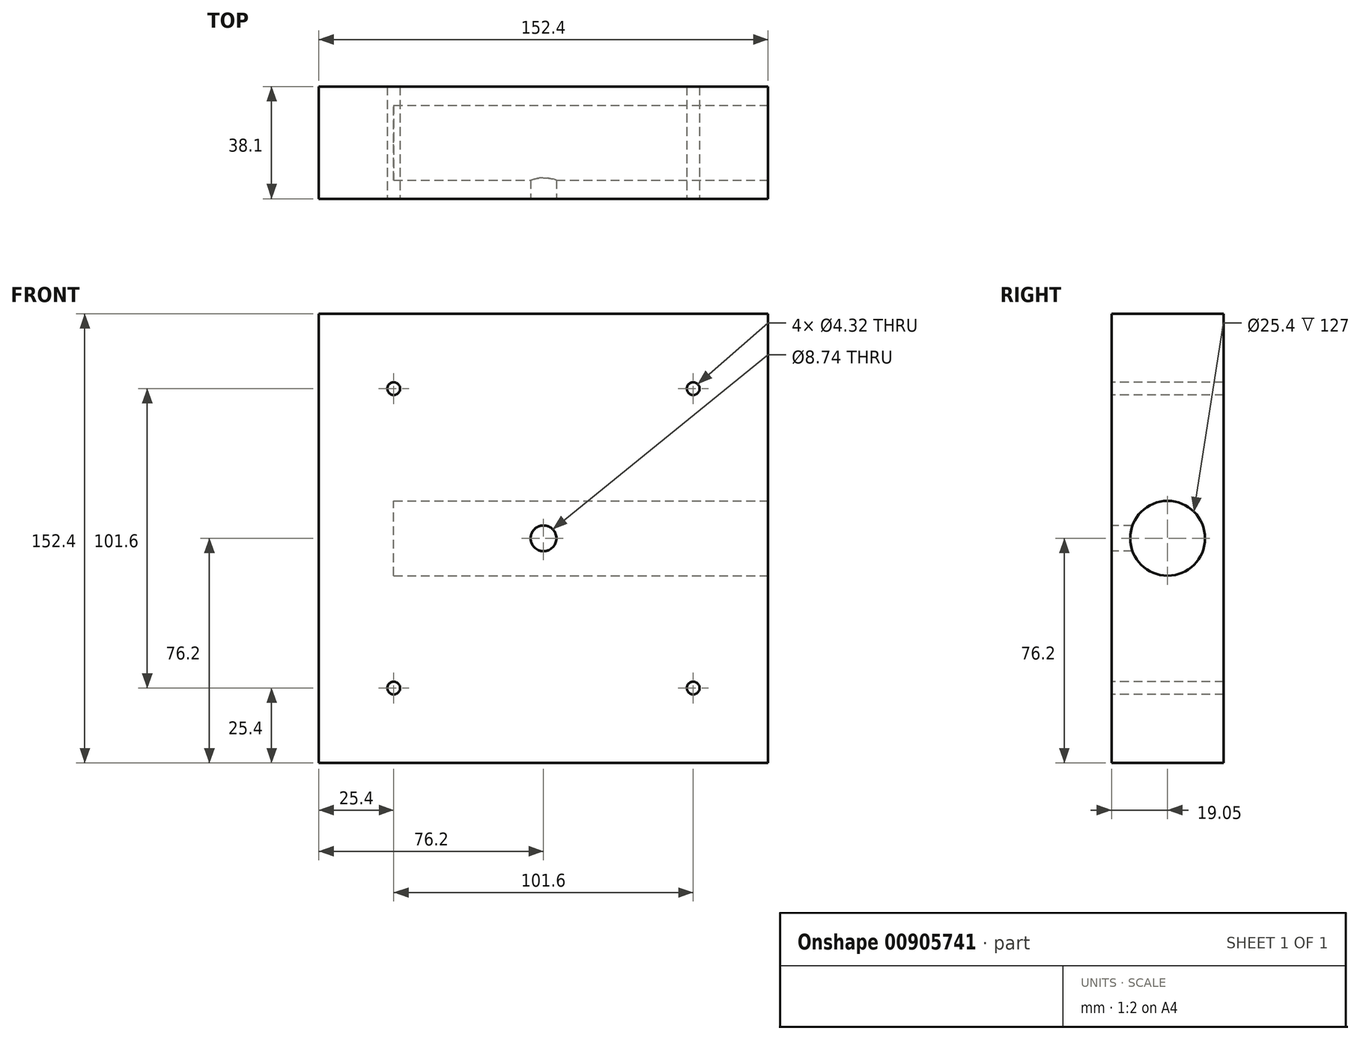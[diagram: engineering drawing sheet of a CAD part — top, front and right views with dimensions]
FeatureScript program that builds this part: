
annotation { "Feature Type Name" : "Feature", "Feature Type Description" : "" }
export const myFeature = defineFeature(function(context is Context, id is Id, definition is map)
    precondition{}
    {
        {
            var Q0;
            Q0=qCreatedBy(makeId("Front.planeOp"),FACE);
            var sketch = newSketch(context, id + "F0", { "sketchPlane" : qUnion([Q0])});
            skLineSegment(sketch, "E0.bottom", {"start": v(76.2, -76.2) * mm, "end": v(-76.2, -76.2) * mm});
            skLineSegment(sketch, "E0.top", {"start": v(76.2, 76.2) * mm, "end": v(-76.2, 76.2) * mm});
            skLineSegment(sketch, "E0.left", {"start": v(76.2, -76.2) * mm, "end": v(76.2, 76.2) * mm});
            skLineSegment(sketch, "E0.right", {"start": v(-76.2, -76.2) * mm, "end": v(-76.2, 76.2) * mm});
            skPoint(sketch, "E0.middle", {"position": v(0, 0) * mm});
            skSolve(sketch);
        }
        {
            var Q0;
            Q0=makeQuery(id+"F0.imprint","IMPRINT",FACE,{"disambiguationData":[TD([[makeQuery(id+"F0.imprint","IMPRINT",EDGE,{"derivedFrom":sQuery(id+"F0.wireOp",EDGE,"E0.bottom")}),-1.0]])]});
            extrude(context, id + "F1", {"entities" : qUnion([Q0]), "depth" : 38.1 * mm, "offsetDistance" : 25.4 * mm});
        }
        {
            var Q0;
            Q0=makeQuery(id+"F1.opExtrude","SWEPT_FACE",FACE,{"disambiguationData":[OSD([sQuery(id+"F0.wireOp",EDGE,"E0.left")])]});
            var sketch = newSketch(context, id + "F2", { "sketchPlane" : qUnion([Q0])});
            skCircle(sketch, "E1", {"center": v(-19.05, 0) * mm, "radius": 12.7 * mm});
            skPoint(sketch, "E1.centerSnap0", {"position": v(-19.05, 76.2) * mm});
            skSolve(sketch);
        }
        {
            var Q0;
            Q0=makeQuery(id+"F1.opExtrude","CAP_FACE",FACE,{"disambiguationData":[OSD([sQuery(id+"F0.wireOp",EDGE,"E0.bottom"),sQuery(id+"F0.wireOp",EDGE,"E0.top"),sQuery(id+"F0.wireOp",EDGE,"E0.left"),sQuery(id+"F0.wireOp",EDGE,"E0.right")])],"isStart":false});
            var sketch = newSketch(context, id + "F3", { "sketchPlane" : qUnion([Q0])});
            skCircle(sketch, "E2", {"center": v(0, 0) * mm, "radius": 1.27 * mm});
            skSolve(sketch);
        }
        {
            var Q0;
            Q0=sQuery(id+"F3.wireOp",VERTEX,"E2.center");
            var Q1;
            Q1=makeQuery(id+"F1.opExtrude","SWEPT_BODY",BODY,{"disambiguationData":[OSD([sQuery(id+"F0.wireOp",EDGE,"E0.bottom"),sQuery(id+"F0.wireOp",EDGE,"E0.top"),sQuery(id+"F0.wireOp",EDGE,"E0.left"),sQuery(id+"F0.wireOp",EDGE,"E0.right")])]});
            hole(context, id + "F4", {"style" : HoleStyle.SIMPLE, "endStyle" : HoleEndStyle.BLIND, "standardTappedOrClearance" : lookupTablePath({ "fit" : "Normal (ASME)", "standard" : "ANSI", "size" : "5/16", "type" : "Clearance" }), "standardBlindInLast" : lookupTablePath({ "fit" : "Normal", "standard" : "ANSI", "size" : "5/16", "type" : "Clearance" }), "holeDiameter" : 8.74 * mm, "majorDiameter" : 6.35 * mm, "holeDepth" : 12.7 * mm, "isTappedThrough" : true, "tappedDepth" : 12.7 * mm, "tapClearance" : 3, "locations" : qUnion([Q0]), "scope" : qUnion([Q1])});
        }
        {
            var Q0;
            Q0=makeQuery(id+"F2.imprint","IMPRINT",FACE,{"disambiguationData":[TD([[makeQuery(id+"F2.imprint","IMPRINT",EDGE,{"derivedFrom":sQuery(id+"F2.wireOp",EDGE,"E1")}),1.0]])]});
            extrude(context, id + "F5", {"entities" : qUnion([Q0]), "operationType" : NewBodyOperationType.REMOVE, "oppositeDirection" : true, "depth" : 127 * mm, "offsetDistance" : 25.4 * mm});
        }
        {
            var Q0;
            Q0=makeQuery(id+"F1.opExtrude","CAP_FACE",FACE,{"disambiguationData":[OSD([sQuery(id+"F0.wireOp",EDGE,"E0.bottom"),sQuery(id+"F0.wireOp",EDGE,"E0.top"),sQuery(id+"F0.wireOp",EDGE,"E0.left"),sQuery(id+"F0.wireOp",EDGE,"E0.right")])],"isStart":false});
            var sketch = newSketch(context, id + "F6", { "sketchPlane" : qUnion([Q0])});
            skCircle(sketch, "E3", {"center": v(-50.8, 50.8) * mm, "radius": 1.27 * mm});
            skCircle(sketch, "E4", {"center": v(50.8, 50.8) * mm, "radius": 1.27 * mm});
            skCircle(sketch, "E5", {"center": v(-50.8, -50.8) * mm, "radius": 1.27 * mm});
            skCircle(sketch, "E6", {"center": v(50.8, -50.8) * mm, "radius": 1.27 * mm});
            skSolve(sketch);
        }
        {
            var Q0;
            Q0=sQuery(id+"F6.wireOp",VERTEX,"E3.center");
            var Q1;
            Q1=sQuery(id+"F6.wireOp",VERTEX,"E4.center");
            var Q2;
            Q2=sQuery(id+"F6.wireOp",VERTEX,"E5.center");
            var Q3;
            Q3=sQuery(id+"F6.wireOp",VERTEX,"E6.center");
            var Q4;
            Q4=makeQuery(id+"F1.opExtrude","SWEPT_BODY",BODY,{"disambiguationData":[OSD([sQuery(id+"F0.wireOp",EDGE,"E0.bottom"),sQuery(id+"F0.wireOp",EDGE,"E0.top"),sQuery(id+"F0.wireOp",EDGE,"E0.left"),sQuery(id+"F0.wireOp",EDGE,"E0.right")])]});
            hole(context, id + "F7", {"style" : HoleStyle.SIMPLE, "endStyle" : HoleEndStyle.BLIND, "standardTappedOrClearance" : lookupTablePath({ "fit" : "Normal (ASME)", "standard" : "ANSI", "size" : "#6", "type" : "Clearance" }), "standardBlindInLast" : lookupTablePath({ "fit" : "Normal", "standard" : "ANSI", "size" : "#6", "type" : "Clearance" }), "holeDiameter" : 4.32 * mm, "majorDiameter" : 6.35 * mm, "holeDepth" : 38.1 * mm, "isTappedThrough" : true, "tappedDepth" : 12.7 * mm, "tapClearance" : 3, "locations" : qUnion([Q0, Q1, Q2, Q3]), "scope" : qUnion([Q4])});
        }
    });
